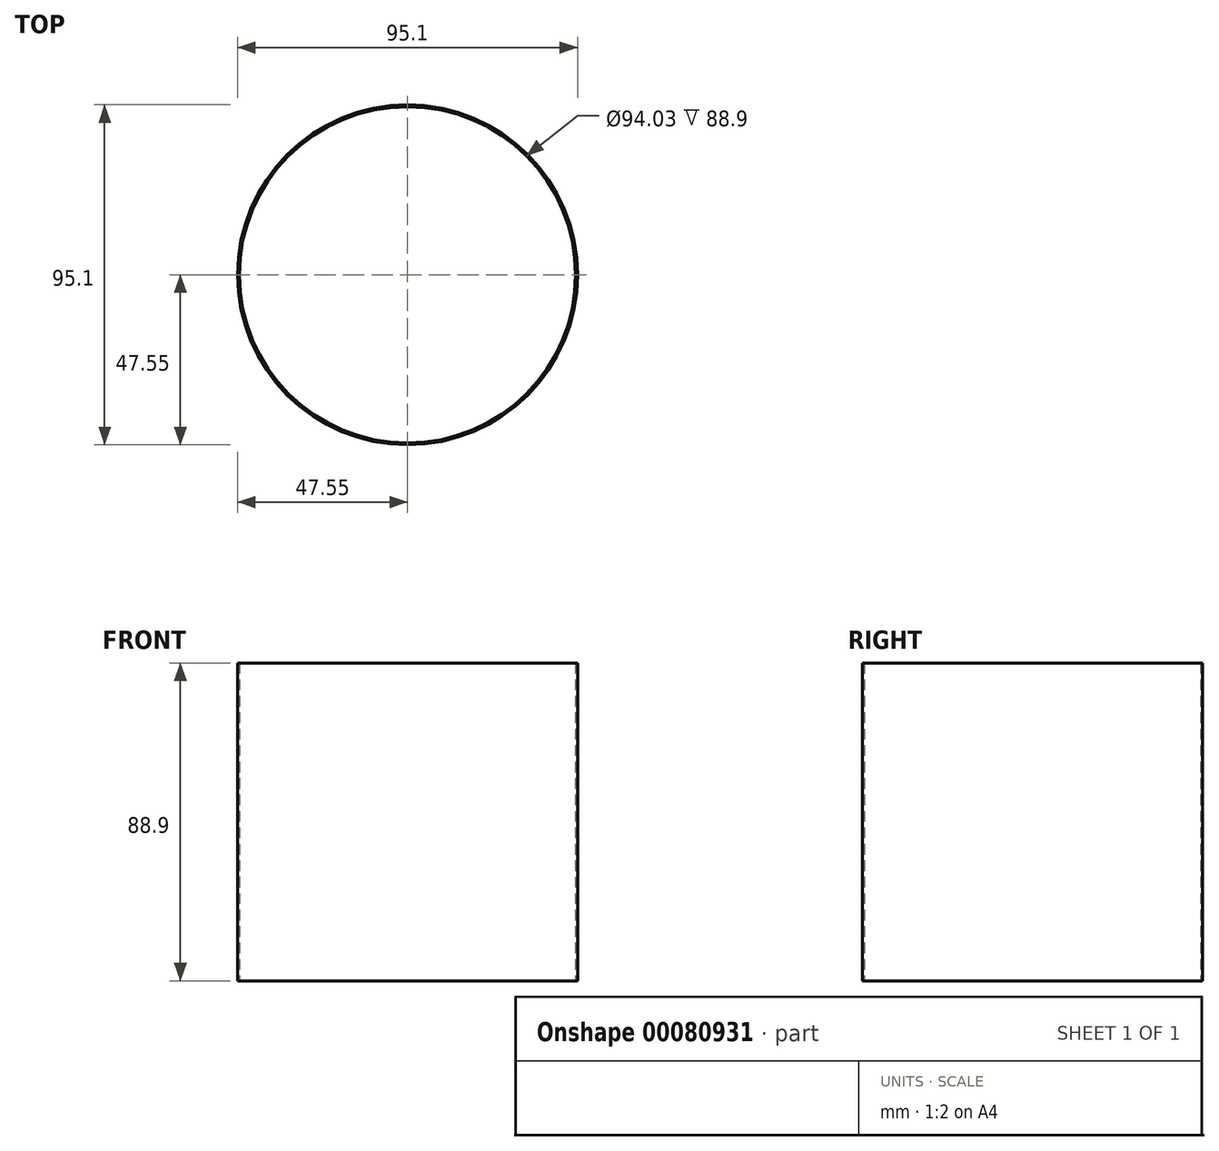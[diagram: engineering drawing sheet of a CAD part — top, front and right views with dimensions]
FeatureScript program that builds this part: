
annotation { "Feature Type Name" : "Feature", "Feature Type Description" : "" }
export const myFeature = defineFeature(function(context is Context, id is Id, definition is map)
    precondition{}
    {
        {
            var Q0;
            Q0=qCreatedBy(makeId("Top.planeOp"),FACE);
            var sketch = newSketch(context, id + "F0", { "sketchPlane" : qUnion([Q0])});
            skCircle(sketch, "E0", {"center": v(0, 0) * mm, "radius": 47.55 * mm});
            skCircle(sketch, "E1", {"center": v(0, 0) * mm, "radius": 47.02 * mm});
            skSolve(sketch);
        }
        {
            var Q0;
            Q0=makeQuery(id+"F0.imprint","IMPRINT",FACE,{"disambiguationData":[TD([[makeQuery(id+"F0.imprint","IMPRINT",EDGE,{"derivedFrom":sQuery(id+"F0.wireOp",EDGE,"E0")}),1.0]])]});
            extrude(context, id + "F1", {"entities" : qUnion([Q0]), "depth" : 88.9 * mm, "offsetDistance" : 25.4 * mm});
        }
    });
